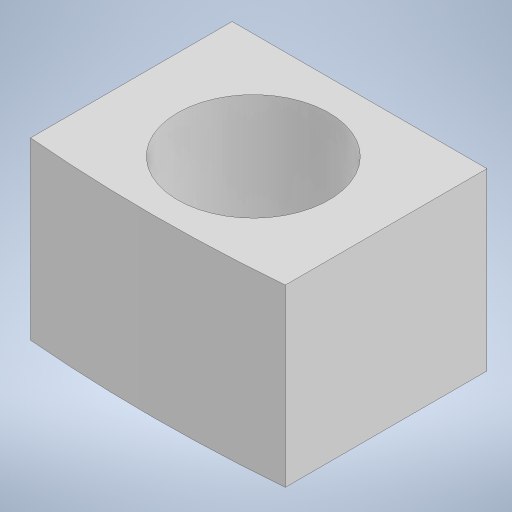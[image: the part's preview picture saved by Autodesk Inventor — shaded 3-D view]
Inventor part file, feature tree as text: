
AUTODESK INVENTOR PART (.ipt)
format: ipt  version: 2024 (Build 280153000, 153)  size: 482,304 bytes
history: native  units: mm
features: extrude x1, sketch x1
ambient origin geometry x8: Origin, YZ Plane, XZ Plane, XY Plane, X Axis, Y Axis, Z Axis, Center Point
bodies: Solid1 (feature_tree)
feature tree (2):
  extrude  "Extrusion1"  Depth=5.5mm
  sketch  "Sketch1"  dims[d0=100.0mm d1=93.0mm d2=4.75mm d6=40.0mm d8=4.0mm d10=4.0mm d11=4.0mm d12=0.0mm d13=5.5mm d14=0.0mm]
